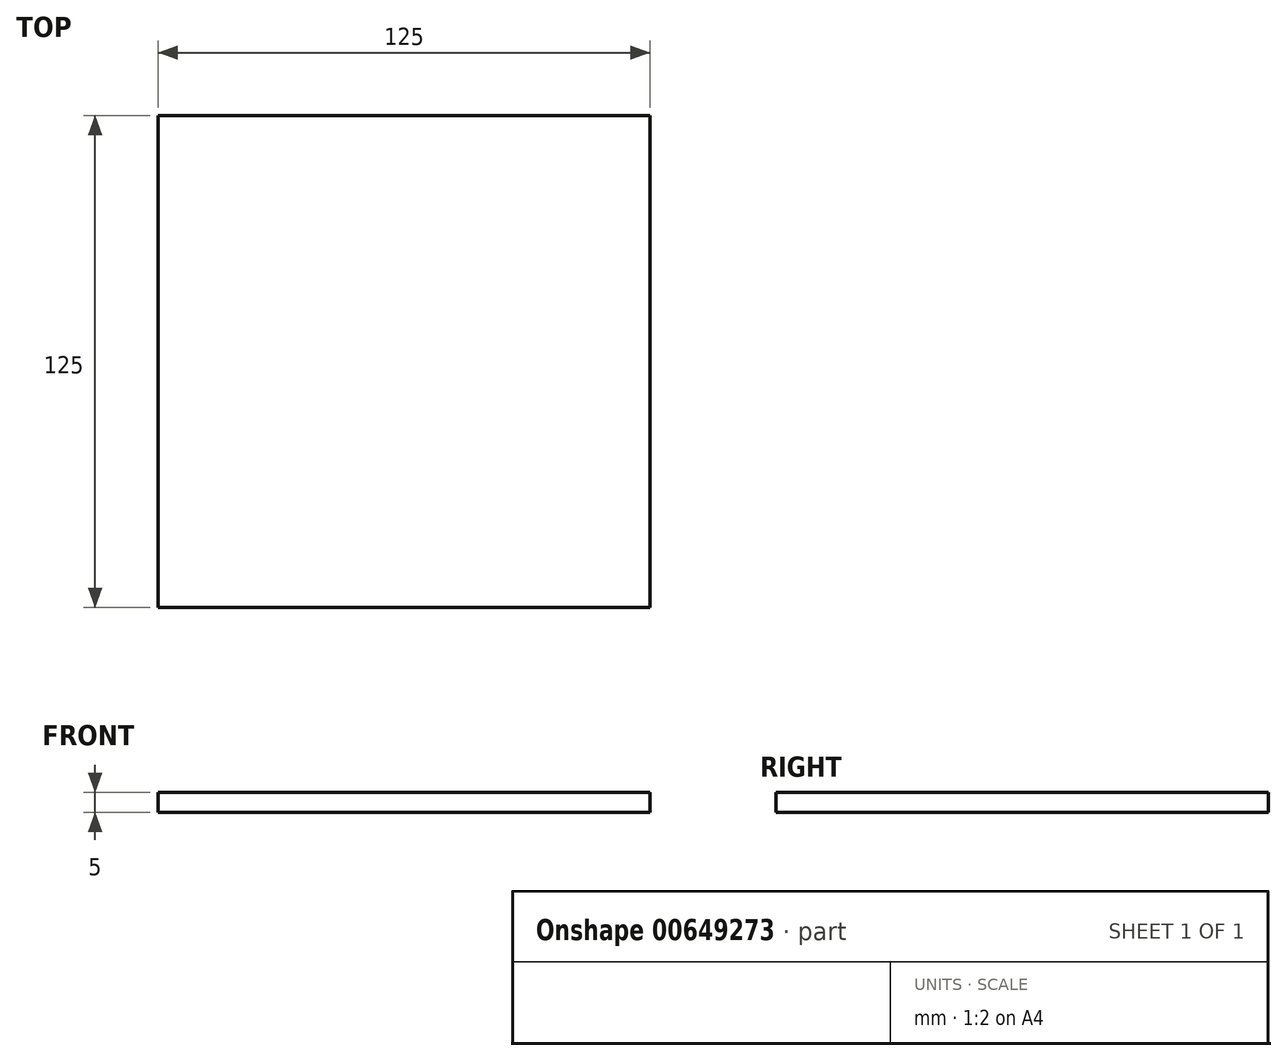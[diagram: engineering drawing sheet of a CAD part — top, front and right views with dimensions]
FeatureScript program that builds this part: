
annotation { "Feature Type Name" : "Feature", "Feature Type Description" : "" }
export const myFeature = defineFeature(function(context is Context, id is Id, definition is map)
    precondition{}
    {
        {
            var Q0;
            Q0=qCreatedBy(makeId("Top.planeOp"),FACE);
            var sketch = newSketch(context, id + "F0", { "sketchPlane" : qUnion([Q0])});
            skLineSegment(sketch, "E0.bottom", {"start": v(-79.89, 61.38) * mm, "end": v(45.11, 61.38) * mm});
            skLineSegment(sketch, "E0.top", {"start": v(-79.89, -63.62) * mm, "end": v(45.11, -63.62) * mm});
            skLineSegment(sketch, "E0.left", {"start": v(-79.89, 61.38) * mm, "end": v(-79.89, -63.62) * mm});
            skLineSegment(sketch, "E0.right", {"start": v(45.11, 61.38) * mm, "end": v(45.11, -63.62) * mm});
            skSolve(sketch);
        }
        {
            var Q0;
            Q0=makeQuery(id+"F0.imprint","IMPRINT",FACE,{"disambiguationData":[TD([[makeQuery(id+"F0.imprint","IMPRINT",EDGE,{"derivedFrom":sQuery(id+"F0.wireOp",EDGE,"E0.bottom")}),-1.0]])]});
            extrude(context, id + "F1", {"entities" : qUnion([Q0]), "depth" : 5 * mm, "offsetDistance" : 25 * mm});
        }
    });
